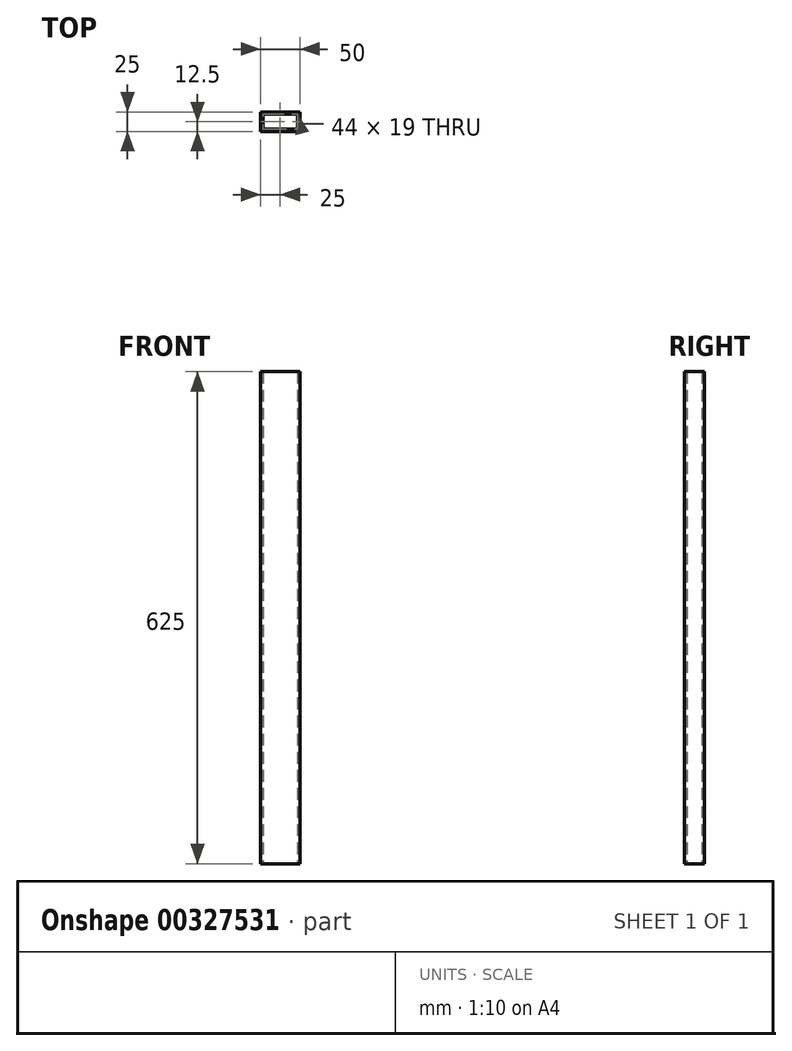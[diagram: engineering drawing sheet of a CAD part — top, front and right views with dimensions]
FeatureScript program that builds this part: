
annotation { "Feature Type Name" : "Feature", "Feature Type Description" : "" }
export const myFeature = defineFeature(function(context is Context, id is Id, definition is map)
    precondition{}
    {
        {
            var Q0;
            Q0=qCreatedBy(makeId("Top.planeOp"),FACE);
            var sketch = newSketch(context, id + "F0", { "sketchPlane" : qUnion([Q0])});
            skLineSegment(sketch, "E0.bottom", {"start": v(-25, -12.5) * mm, "end": v(25, -12.5) * mm});
            skLineSegment(sketch, "E0.top", {"start": v(-25, 12.5) * mm, "end": v(25, 12.5) * mm});
            skLineSegment(sketch, "E0.left", {"start": v(-25, -12.5) * mm, "end": v(-25, 12.5) * mm});
            skLineSegment(sketch, "E0.right", {"start": v(25, -12.5) * mm, "end": v(25, 12.5) * mm});
            skPoint(sketch, "E0.middle", {"position": v(0, 0) * mm});
            skLineSegment(sketch, "E1.bottom", {"start": v(-22, -9.5) * mm, "end": v(22, -9.5) * mm});
            skLineSegment(sketch, "E1.top", {"start": v(-22, 9.5) * mm, "end": v(22, 9.5) * mm});
            skLineSegment(sketch, "E1.left", {"start": v(-22, -9.5) * mm, "end": v(-22, 9.5) * mm});
            skLineSegment(sketch, "E1.right", {"start": v(22, -9.5) * mm, "end": v(22, 9.5) * mm});
            skSolve(sketch);
        }
        {
            var Q0;
            Q0=makeQuery(id+"F0.imprint","IMPRINT",FACE,{"disambiguationData":[TD([[makeQuery(id+"F0.imprint","IMPRINT",EDGE,{"derivedFrom":sQuery(id+"F0.wireOp",EDGE,"E0.bottom")}),1.0]])]});
            extrude(context, id + "F1", {"entities" : qUnion([Q0]), "depth" : 625 * mm, "symmetric" : true});
        }
    });
